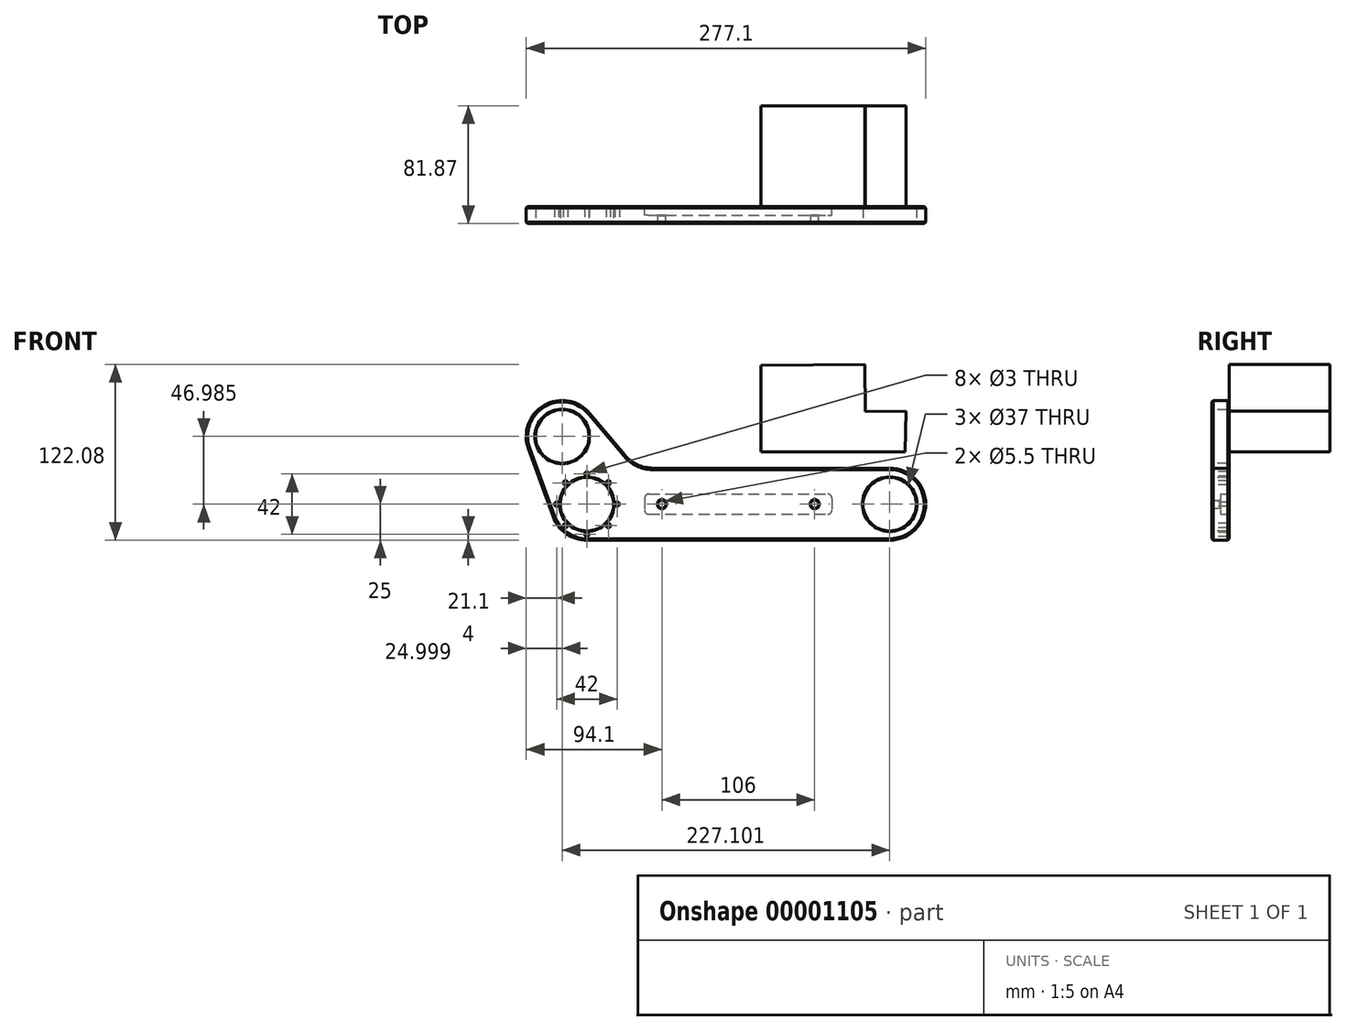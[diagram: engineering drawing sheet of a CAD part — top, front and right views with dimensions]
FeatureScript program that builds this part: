
annotation { "Feature Type Name" : "Feature", "Feature Type Description" : "" }
export const myFeature = defineFeature(function(context is Context, id is Id, definition is map)
    precondition{}
    {
        {
            var Q0;
            Q0=qCreatedBy(makeId("Front.planeOp"),FACE);
            var sketch = newSketch(context, id + "F0", { "sketchPlane" : qUnion([Q0])});
            skLineSegment(sketch, "E0", {"start": v(0, -25) * mm, "end": v(210, -25) * mm});
            skArc(sketch, "E1", {"start": v(210, -25) * mm, "mid": v(235, 0) * mm, "end": v(210, 25) * mm});
            skLineSegment(sketch, "E2", {"start": v(210, 25) * mm, "end": v(45.64, 25) * mm});
            skLineSegment(sketch, "E3", {"start": v(26.49, 33.93) * mm, "end": v(2.05, 63.05) * mm});
            skArc(sketch, "E4", {"start": v(2.05, 63.05) * mm, "mid": v(-29.6, 68.64) * mm, "end": v(-40.6, 38.43) * mm});
            skLineSegment(sketch, "E5", {"start": v(-40.6, 38.43) * mm, "end": v(-23.5, -8.55) * mm});
            skPoint(sketch, "E6.visualSharp", {"position": v(-17.5, -25) * mm});
            skArc(sketch, "E6.filletArc", {"start": v(-23.5, -8.55) * mm, "mid": v(-14.34, -20.48) * mm, "end": v(0, -25) * mm});
            skLineSegment(sketch, "E7", {"start": v(-17.1, 46.98) * mm, "end": v(0, 0) * mm, "construction": true});
            skPoint(sketch, "E8.visualSharp", {"position": v(33.98, 25) * mm});
            skArc(sketch, "E8.filletArc", {"start": v(26.49, 33.93) * mm, "mid": v(35.07, 27.34) * mm, "end": v(45.64, 25) * mm});
            skSolve(sketch);
        }
        {
            var Q0;
            Q0=makeQuery(id+"F0.imprint","IMPRINT",FACE,{"disambiguationData":[TD([[makeQuery(id+"F0.imprint","IMPRINT",EDGE,{"derivedFrom":sQuery(id+"F0.wireOp",EDGE,"E0")}),1.0]])]});
            extrude(context, id + "F1", {"entities" : qUnion([Q0]), "endBound" : BoundingType.SYMMETRIC, "depth" : 12 * mm});
        }
        {
            var Q0;
            Q0=makeQuery(id+"F1.opExtrude","CAP_FACE",FACE,{"disambiguationData":[OSD([sQuery(id+"F0.wireOp",EDGE,"E0"),sQuery(id+"F0.wireOp",EDGE,"E1"),sQuery(id+"F0.wireOp",EDGE,"E2"),sQuery(id+"F0.wireOp",EDGE,"E3"),sQuery(id+"F0.wireOp",EDGE,"E4"),sQuery(id+"F0.wireOp",EDGE,"E5"),sQuery(id+"F0.wireOp",EDGE,"E6.filletArc"),sQuery(id+"F0.wireOp",EDGE,"E8.filletArc")])],"isStart":false});
            var sketch = newSketch(context, id + "F2", { "sketchPlane" : qUnion([Q0])});
            skCircle(sketch, "E9", {"center": v(-17.1, 46.98) * mm, "radius": 18.5 * mm});
            skCircle(sketch, "E10", {"center": v(0, 0) * mm, "radius": 18.5 * mm});
            skCircle(sketch, "E11", {"center": v(210, 0) * mm, "radius": 18.5 * mm});
            skSolve(sketch);
        }
        {
            var Q0;
            {Q0=qUnion([makeQuery(id+"F2.imprint","IMPRINT",FACE,{"disambiguationData":[TD([[makeQuery(id+"F2.imprint","IMPRINT",EDGE,{"derivedFrom":sQuery(id+"F2.wireOp",EDGE,"E9")}),1.0]])]}),makeQuery(id+"F2.imprint","IMPRINT",FACE,{"disambiguationData":[TD([[makeQuery(id+"F2.imprint","IMPRINT",EDGE,{"derivedFrom":sQuery(id+"F2.wireOp",EDGE,"E10")}),1.0]])]}),makeQuery(id+"F2.imprint","IMPRINT",FACE,{"disambiguationData":[TD([[makeQuery(id+"F2.imprint","IMPRINT",EDGE,{"derivedFrom":sQuery(id+"F2.wireOp",EDGE,"E11")}),1.0]])]})]);}
            extrude(context, id + "F3", {"entities" : qUnion([Q0]), "operationType" : NewBodyOperationType.REMOVE, "endBound" : BoundingType.UP_TO_NEXT, "oppositeDirection" : true, "depth" : 25 * mm});
        }
        {
            var Q0;
            Q0=makeQuery(id+"F1.opExtrude","CAP_FACE",FACE,{"disambiguationData":[OSD([sQuery(id+"F0.wireOp",EDGE,"E0"),sQuery(id+"F0.wireOp",EDGE,"E1"),sQuery(id+"F0.wireOp",EDGE,"E2"),sQuery(id+"F0.wireOp",EDGE,"E3"),sQuery(id+"F0.wireOp",EDGE,"E4"),sQuery(id+"F0.wireOp",EDGE,"E5"),sQuery(id+"F0.wireOp",EDGE,"E6.filletArc"),sQuery(id+"F0.wireOp",EDGE,"E8.filletArc")])],"isStart":true});
            var sketch = newSketch(context, id + "F4", { "sketchPlane" : qUnion([Q0])});
            skLineSegment(sketch, "E12.bottom", {"start": v(-40, 7) * mm, "end": v(-170, 7) * mm});
            skLineSegment(sketch, "E12.top", {"start": v(-40, -7) * mm, "end": v(-170, -7) * mm});
            skLineSegment(sketch, "E12.left", {"start": v(-40, 7) * mm, "end": v(-40, -7) * mm});
            skLineSegment(sketch, "E12.right", {"start": v(-170, 7) * mm, "end": v(-170, -7) * mm});
            skPoint(sketch, "E13", {"position": v(-210, 0) * mm});
            skSolve(sketch);
        }
        {
            var Q0;
            Q0=makeQuery(id+"F4.imprint","IMPRINT",FACE,{"disambiguationData":[TD([[makeQuery(id+"F4.imprint","IMPRINT",EDGE,{"derivedFrom":sQuery(id+"F4.wireOp",EDGE,"E12.bottom")}),1.0]])]});
            extrude(context, id + "F5", {"entities" : qUnion([Q0]), "operationType" : NewBodyOperationType.REMOVE, "oppositeDirection" : true, "depth" : 6 * mm});
        }
        {
            var Q0;
            Q0=makeQuery(id+"F5.boolean.opBoolean","COPY",EDGE,{"derivedFrom":makeQuery(id+"F5.opExtrude","SWEPT_EDGE",EDGE,{"disambiguationData":[OSD([sQuery(id+"F4.wireOp",EDGE,"E12.bottom"),sQuery(id+"F4.wireOp",EDGE,"E12.left")])]})});
            var Q1;
            Q1=makeQuery(id+"F5.boolean.opBoolean","COPY",EDGE,{"derivedFrom":makeQuery(id+"F5.opExtrude","SWEPT_EDGE",EDGE,{"disambiguationData":[OSD([sQuery(id+"F4.wireOp",EDGE,"E12.top"),sQuery(id+"F4.wireOp",EDGE,"E12.left")])]})});
            var Q2;
            Q2=makeQuery(id+"F5.boolean.opBoolean","COPY",EDGE,{"derivedFrom":makeQuery(id+"F5.opExtrude","SWEPT_EDGE",EDGE,{"disambiguationData":[OSD([sQuery(id+"F4.wireOp",EDGE,"E12.top"),sQuery(id+"F4.wireOp",EDGE,"E12.right")])]})});
            var Q3;
            Q3=makeQuery(id+"F5.boolean.opBoolean","COPY",EDGE,{"derivedFrom":makeQuery(id+"F5.opExtrude","SWEPT_EDGE",EDGE,{"disambiguationData":[OSD([sQuery(id+"F4.wireOp",EDGE,"E12.bottom"),sQuery(id+"F4.wireOp",EDGE,"E12.right")])]})});
            fillet(context, id + "F6", {"entities" : qUnion([Q0, Q1, Q2, Q3]), "radius" : 3 * mm, "tangentPropagation" : true, "allowEdgeOverflow" : false});
        }
        {
            var Q0;
            Q0=makeQuery(id+"F5.boolean.opBoolean","COPY",FACE,{"derivedFrom":makeQuery(id+"F5.opExtrude","CAP_FACE",FACE,{"disambiguationData":[OSD([sQuery(id+"F4.wireOp",EDGE,"E12.bottom"),sQuery(id+"F4.wireOp",EDGE,"E12.top"),sQuery(id+"F4.wireOp",EDGE,"E12.left"),sQuery(id+"F4.wireOp",EDGE,"E12.right")])],"isStart":false})});
            var sketch = newSketch(context, id + "F7", { "sketchPlane" : qUnion([Q0])});
            skCircle(sketch, "E14", {"center": v(-158, 0) * mm, "radius": 2.75 * mm});
            skCircle(sketch, "E15", {"center": v(-52, 0) * mm, "radius": 2.75 * mm});
            skSolve(sketch);
        }
        {
            var Q0;
            {Q0=qUnion([makeQuery(id+"F7.imprint","IMPRINT",FACE,{"disambiguationData":[TD([[makeQuery(id+"F7.imprint","IMPRINT",EDGE,{"derivedFrom":sQuery(id+"F7.wireOp",EDGE,"E14")}),1.0]])]}),makeQuery(id+"F7.imprint","IMPRINT",FACE,{"disambiguationData":[TD([[makeQuery(id+"F7.imprint","IMPRINT",EDGE,{"derivedFrom":sQuery(id+"F7.wireOp",EDGE,"E15")}),1.0]])]})]);}
            extrude(context, id + "F8", {"entities" : qUnion([Q0]), "operationType" : NewBodyOperationType.REMOVE, "endBound" : BoundingType.UP_TO_NEXT, "oppositeDirection" : true, "depth" : 25 * mm});
        }
        {
            var Q0;
            Q0=makeQuery(id+"F1.opExtrude","CAP_FACE",FACE,{"disambiguationData":[OSD([sQuery(id+"F0.wireOp",EDGE,"E0"),sQuery(id+"F0.wireOp",EDGE,"E1"),sQuery(id+"F0.wireOp",EDGE,"E2"),sQuery(id+"F0.wireOp",EDGE,"E3"),sQuery(id+"F0.wireOp",EDGE,"E4"),sQuery(id+"F0.wireOp",EDGE,"E5"),sQuery(id+"F0.wireOp",EDGE,"E6.filletArc"),sQuery(id+"F0.wireOp",EDGE,"E8.filletArc")])],"isStart":false});
            var sketch = newSketch(context, id + "F9", { "sketchPlane" : qUnion([Q0])});
            skCircle(sketch, "E16", {"center": v(14.85, 14.85) * mm, "radius": 1.5 * mm});
            skLineSegment(sketch, "E17", {"start": v(0, 0) * mm, "end": v(14.85, 14.85) * mm, "construction": true});
            skSolve(sketch);
        }
        {
            var Q0;
            Q0=makeQuery(id+"F9.imprint","IMPRINT",FACE,{"disambiguationData":[TD([[makeQuery(id+"F9.imprint","IMPRINT",EDGE,{"derivedFrom":sQuery(id+"F9.wireOp",EDGE,"E16")}),1.0]])]});
            extrude(context, id + "F10", {"entities" : qUnion([Q0]), "operationType" : NewBodyOperationType.REMOVE, "endBound" : BoundingType.UP_TO_NEXT, "oppositeDirection" : true, "depth" : 25 * mm});
        }
        {
            var Q0;
            Q0=makeQuery(id+"F10.boolean.opBoolean","COPY",FACE,{"derivedFrom":makeQuery(id+"F10.opExtrude","SWEPT_FACE",FACE,{"disambiguationData":[OSD([sQuery(id+"F9.wireOp",EDGE,"E16")])]})});
            var Q1;
            Q1=makeQuery(id+"F3.boolean.opBoolean","COPY",FACE,{"derivedFrom":makeQuery(id+"F3.opExtrude","SWEPT_FACE",FACE,{"disambiguationData":[OSD([sQuery(id+"F2.wireOp",EDGE,"E10")])]})});
            circularPattern(context, id + "F11", {"faces" : qUnion([Q0]), "axis" : qUnion([Q1]), "angle" : 45 * degree, "instanceCount" : 8, "patternType" : PatternType.FACE});
        }
        {
            var Q0;
            Q0=makeQuery(id+"F1.opExtrude","CAP_EDGE",EDGE,{"disambiguationData":[OSD([sQuery(id+"F0.wireOp",EDGE,"E4")])],"isStart":false});
            var Q1;
            Q1=makeQuery(id+"F1.opExtrude","CAP_EDGE",EDGE,{"disambiguationData":[OSD([sQuery(id+"F0.wireOp",EDGE,"E5")])],"isStart":true});
            chamfer(context, id + "F12", {"entities" : qUnion([Q0, Q1]), "width" : 1 * mm, "tangentPropagation" : true});
        }
        {
            var Q0;
            Q0=makeQuery(id+"F5.boolean.opBoolean","COPY",EDGE,{"derivedFrom":makeQuery(id+"F5.opExtrude","CAP_EDGE",EDGE,{"disambiguationData":[OSD([sQuery(id+"F4.wireOp",EDGE,"E12.bottom")])],"isStart":true})});
            var Q1;
            Q1=makeQuery(id+"F3.boolean.opBoolean","COPY",FACE,{"derivedFrom":makeQuery(id+"F3.opExtrude","SWEPT_FACE",FACE,{"disambiguationData":[OSD([sQuery(id+"F2.wireOp",EDGE,"E11")])]})});
            var Q2;
            Q2=makeQuery(id+"F3.boolean.opBoolean","COPY",FACE,{"derivedFrom":makeQuery(id+"F3.opExtrude","SWEPT_FACE",FACE,{"disambiguationData":[OSD([sQuery(id+"F2.wireOp",EDGE,"E10")])]})});
            var Q3;
            Q3=makeQuery(id+"F3.boolean.opBoolean","COPY",FACE,{"derivedFrom":makeQuery(id+"F3.opExtrude","SWEPT_FACE",FACE,{"disambiguationData":[OSD([sQuery(id+"F2.wireOp",EDGE,"E9")])]})});
            var Q4;
            Q4=makeQuery(id+"F8.boolean.opBoolean","COPY",FACE,{"derivedFrom":makeQuery(id+"F8.opExtrude","SWEPT_FACE",FACE,{"disambiguationData":[OSD([sQuery(id+"F7.wireOp",EDGE,"E15")])]})});
            var Q5;
            Q5=makeQuery(id+"F8.boolean.opBoolean","COPY",FACE,{"derivedFrom":makeQuery(id+"F8.opExtrude","SWEPT_FACE",FACE,{"disambiguationData":[OSD([sQuery(id+"F7.wireOp",EDGE,"E14")])]})});
            chamfer(context, id + "F13", {"entities" : qUnion([Q0, Q1, Q2, Q3, Q4, Q5]), "width" : .5 * mm, "tangentPropagation" : true});
        }
        {
            var Q0;
            Q0=makeQuery(id+"F1.opExtrude","CAP_FACE",FACE,{"disambiguationData":[OSD([sQuery(id+"F0.wireOp",EDGE,"E0"),sQuery(id+"F0.wireOp",EDGE,"E1"),sQuery(id+"F0.wireOp",EDGE,"E2"),sQuery(id+"F0.wireOp",EDGE,"E3"),sQuery(id+"F0.wireOp",EDGE,"E4"),sQuery(id+"F0.wireOp",EDGE,"E5"),sQuery(id+"F0.wireOp",EDGE,"E6.filletArc"),sQuery(id+"F0.wireOp",EDGE,"E8.filletArc")])],"isStart":true});
            var sketch = newSketch(context, id + "F14", { "sketchPlane" : qUnion([Q0])});
            skLineSegment(sketch, "E18", {"start": v(-220.58, 36.3) * mm, "end": v(-120.58, 36.3) * mm});
            skLineSegment(sketch, "E19", {"start": v(-120.58, 36.3) * mm, "end": v(-120.58, 96.3) * mm});
            skLineSegment(sketch, "E20", {"start": v(-120.58, 96.3) * mm, "end": v(-192.67, 97.08) * mm});
            skLineSegment(sketch, "E21", {"start": v(-192.67, 97.08) * mm, "end": v(-193.14, 64.2) * mm});
            skLineSegment(sketch, "E22", {"start": v(-193.14, 64.2) * mm, "end": v(-221.35, 64.61) * mm});
            skLineSegment(sketch, "E23", {"start": v(-221.35, 64.61) * mm, "end": v(-220.58, 36.3) * mm});
            skSolve(sketch);
        }
        {
            var Q0;
            Q0=makeQuery(id+"F14.imprint","IMPRINT",FACE,{"disambiguationData":[TD([[makeQuery(id+"F14.imprint","IMPRINT",EDGE,{"derivedFrom":sQuery(id+"F14.wireOp",EDGE,"E18")}),1.0]])]});
            extrude(context, id + "F15", {"entities" : qUnion([Q0]), "depth" : 69.87 * mm});
        }
    });
